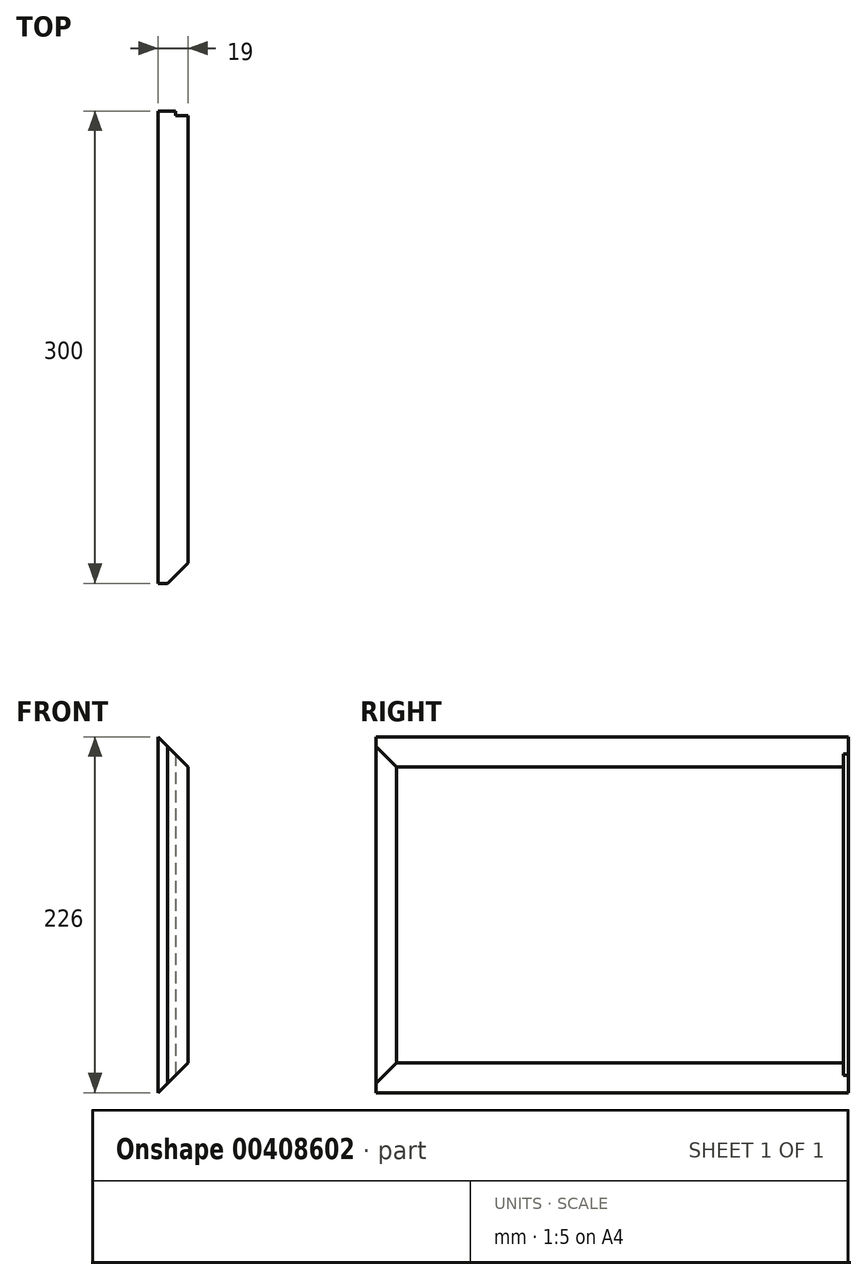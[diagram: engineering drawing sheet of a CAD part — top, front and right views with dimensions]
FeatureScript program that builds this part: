
annotation { "Feature Type Name" : "Feature", "Feature Type Description" : "" }
export const myFeature = defineFeature(function(context is Context, id is Id, definition is map)
    precondition{}
    {
        {
            var Q0;
            Q0=qCreatedBy(makeId("Front.planeOp"),FACE);
            var sketch = newSketch(context, id + "F0", { "sketchPlane" : qUnion([Q0])});
            skLineSegment(sketch, "E0", {"start": v(0, 0) * mm, "end": v(19, 19) * mm});
            skLineSegment(sketch, "E1", {"start": v(19, 19) * mm, "end": v(19, 207) * mm});
            skLineSegment(sketch, "E2", {"start": v(19, 207) * mm, "end": v(0, 226) * mm});
            skLineSegment(sketch, "E3", {"start": v(0, 226) * mm, "end": v(0, 0) * mm});
            skSolve(sketch);
        }
        {
            var Q0;
            Q0 = qSketchRegion(id + "F0", true);
            extrude(context, id + "F1", {"entities" : qUnion([Q0]), "depth" : 300 * mm});
        }
        {
            var Q0;
            Q0=makeQuery(id+"F1.opExtrude","CAP_EDGE",EDGE,{"disambiguationData":[OSD([sQuery(id+"F0.wireOp",EDGE,"E1")])],"isStart":false});
            chamfer(context, id + "F2", {"entities" : qUnion([Q0]), "width" : 13 * mm, "tangentPropagation" : true});
        }
        {
            var Q0;
            Q0=makeQuery(id+"F1.opExtrude","CAP_FACE",FACE,{"disambiguationData":[OSD([sQuery(id+"F0.wireOp",EDGE,"E0"),sQuery(id+"F0.wireOp",EDGE,"E1"),sQuery(id+"F0.wireOp",EDGE,"E2"),sQuery(id+"F0.wireOp",EDGE,"E3")])],"isStart":true});
            var sketch = newSketch(context, id + "F3", { "sketchPlane" : qUnion([Q0])});
            skPoint(sketch, "E4.oppositeSnap0", {"position": v(-11, 211.02) * mm});
            skLineSegment(sketch, "E4.bottom", {"start": v(-19, 300) * mm, "end": v(-11, 300) * mm});
            skLineSegment(sketch, "E4.top", {"start": v(-19, 0) * mm, "end": v(-11, 0) * mm});
            skLineSegment(sketch, "E4.left", {"start": v(-19, 300) * mm, "end": v(-19, 0) * mm});
            skLineSegment(sketch, "E4.right", {"start": v(-11, 300) * mm, "end": v(-11, 0) * mm});
            skSolve(sketch);
        }
        {
            var Q0;
            Q0 = qSketchRegion(id + "F3", true);
            extrude(context, id + "F4", {"entities" : qUnion([Q0]), "operationType" : NewBodyOperationType.REMOVE, "oppositeDirection" : true, "depth" : 3 * mm});
        }
    });
